# Revit family: D SONNIGER - HEATER CONDENS - CR ONE, CR1, CR2, CR3, CR3 MAX, CR4 MAX
name_source: partatom
category: Wyposażenie mechaniczne
revit_build: Autodesk Revit 2018 (Build: 20170927_1515(x64)
units: mm (PartAtom-declared; Revit-internal decimal feet)

## family parameters
Klasyfikacja = Brak
Obiekt nadrzędny = Powierzchnia
Punkt obliczania pomieszczeń = Nie
Tnij formami wycięć po wczytaniu = Nie
Typ części = Normalny
Współdzielony = Nie
Wymiar okrągłego złącza = Użyj średnicy

## types (14) — shared parameters
Autor = www.archispace.com
Betriebsspannung = 230 V
Domyślna rzędna = 1219.200 mm
Material = 230,230,230
Maximaler Arbeitsdruck = 1600000.0 Pa
Motor IP = IP54
O = 130.000 mm
Opis = Wasserlufterhitzer
Producent = SONNIGER Polska Sp. z o.o. Sp. k.
max. Temparatur des Heizmittels = 120 °C
zero-valued in all types: Arbeitsniveau

## per-type parameters (varying)
| type | Anzahl der Heizreihen | Gewicht / befüllt | Gewicht / unbefüllt | H | Lärmpegel | Maximale Heizleistung | Maximale Luftleistung | Maximaler Strahlbereich | Minimale Heizleistung | Model | Motordrehzahl | Motorstärke | O1 | S g | W g | ΔT |
| CR ONE - Wandmontage | 2 | 10.70 kg | 9.60 kg | 18536.143 mm | I. Stufe 35 dB / II. Stufe 46 dB / III. Stufe 52 dB Geschwindigkeit | 25 kW | 1600.0 m³/h | 14000.000 mm | 5 kW | Heater CONDENS CR ONE | 1400 | 124 W | Tak | 13120.000 mm | 13850.000 mm | 25 °C |
| CR1 - Wandmontage | 1 | 11.90 kg | 10.80 kg | 26136.143 mm | I. Stufe 44 dB / II. Stufe 52 dB / III. Stufe 62 dB Geschwindigkeit | 35 kW | 3900.0 m³/h | 24000.000 mm | 10 kW | Heater CONDENS CR1 | 1350 | 250 W | Tak | 16000.000 mm | 16000.000 mm | 13 °C |
| CR2 - Wandmontage | 2 | 14.80 kg | 12.70 kg | 24536.143 mm | I. Stufe 41 dB / II. Stufe 50 dB / III. Stufe 60 dB Geschwindigkeit | 50 kW | 3350.0 m³/h | 21000.000 mm | 15 kW | Heater CONDENS CR2 | 1350 | 250 W | Tak | 15900.000 mm | 15100.000 mm | 22 °C |
| CR3 - Wandmontage | 3 | 16.90 kg | 14.50 kg | 22936.143 mm | I. Stufe 39 dB / II. Stufe 48 dB / III. Stufe 58 dB Geschwindigkeit | 70 kW | 2950.0 m³/h | 19000.000 mm | 20 kW | Heater CONDENS CR3 | 1350 | 250 W | Tak | 15400.000 mm | 14600.000 mm | 34 °C |
| CR ONE - Deckenmontage | 2 | 10.70 kg | 9.60 kg | 9536.143 mm | I. Stufe 35 dB / II. Stufe 46 dB / III. Stufe 52 dB Geschwindigkeit | 25 kW | 1600.0 m³/h | 14000.000 mm | 5 kW | Heater CONDENS CR ONE | 1400 | 124 W | Tak | 9100.000 mm | 9900.000 mm | 25 °C |
| CR1 - Deckenmontage | 1 | 11.90 kg | 10.80 kg | 12536.143 mm | I. Stufe 44 dB / II. Stufe 52 dB / III. Stufe 62 dB Geschwindigkeit | 35 kW | 3900.0 m³/h | 24000.000 mm | 10 kW | Heater CONDENS CR1 | 1350 | 250 W | Tak | 11420.000 mm | 10510.000 mm | 13 °C |
| CR2 - Deckenmontage | 2 | 14.80 kg | 12.70 kg | 11836.143 mm | I. Stufe 41 dB / II. Stufe 50 dB / III. Stufe 60 dB Geschwindigkeit | 50 kW | 3350.0 m³/h | 21000.000 mm | 15 kW | Heater CONDENS CR2 | 1350 | 250 W | Tak | 10900.000 mm | 10360.000 mm | 22 °C |
| CR3 - Deckenmontage | 3 | 16.90 kg | 14.50 kg | 11036.143 mm | I. Stufe 39 dB / II. Stufe 48 dB / III. Stufe 58 dB Geschwindigkeit | 70 kW | 2950.0 m³/h | 19000.000 mm | 20 kW | Heater CONDENS CR3 | 1350 | 250 W | Tak | 10760.000 mm | 9760.000 mm | 34 °C |
| CR2 MAX - Deckenmontage | 2 | 25.20 kg | 23.60 kg | 14860.341 mm | I. Stufe 41 dB / II. Stufe 50 dB / III. Stufe 59 dB Geschwindigkeit | 70 kW | 5700.0 m³/h | 26000.000 mm | 25 kW | Heater CONDENS CR2 MAX | 1380 | 520 W | Nie | 12470.000 mm | 11470.000 mm | 22 °C |
| CR2 MAX - Wandmontage | 2 | 25.20 kg | 23.60 kg | 13536.341 mm | I. Stufe 41 dB / II. Stufe 50 dB / III. Stufe 59 dB Geschwindigkeit | 70 kW | 5700.0 m³/h | 26000.000 mm | 25 kW | Heater CONDENS CR2 MAX | 1380 | 520 W | Nie | 19500.000 mm | 19500.000 mm | 22 °C |
| CR3 MAX - Deckenmontage | 3 | 27.40 kg | 25.20 kg | 14060.341 mm | I. Stufe 40 dB / II. Stufe 48 dB / III. Stufe 58 dB Geschwindigkeit | 95 kW | 5600.0 m³/h | 25000.000 mm | 35 kW | Heater CONDENS CR3 MAX | 1380 | 520 W | Nie | 12000.000 mm | 11250.000 mm | 35 °C |
| CR3 MAX - Wandmontage | 3 | 27.40 kg | 25.50 kg | 31160.341 mm | I. Stufe 40 dB / II. Stufe 48 dB / III. Stufe 58 dB Geschwindigkeit | 95 kW | 5600.0 m³/h | 25000.000 mm | 35 kW | Heater CONDENS CR3 MAX | 1380 | 520 W | Nie | 17900.000 mm | 17100.000 mm | 35 °C |
| CR4 MAX - Deckenmontage | 3 | 28.00 kg | 25.50 kg | 13360.341 mm | I. Stufe 40 dB / II. Stufe 48 dB / III. Stufe 58 dB Geschwindigkeit | 120 kW | 5100.0 m³/h | 23000.000 mm | 40 kW | Heater CONDENS CR4 MAX | 1380 | 520 W | Nie | 11820.000 mm | 10830.000 mm | 44 °C |
| CR4 MAX - Wandmontage | 3 | 28.00 kg | 25.50 kg | 32860.341 mm | I. Stufe 40 dB / II. Stufe 48 dB / III. Stufe 58 dB Geschwindigkeit | 120 kW | 5100.0 m³/h | 23000.000 mm | 40 kW | Heater CONDENS CR4 MAX | 1380 | 520 W | Nie | 18400.000 mm | 17550.000 mm | 44 °C |
